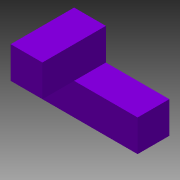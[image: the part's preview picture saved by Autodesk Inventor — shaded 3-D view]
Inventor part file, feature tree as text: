
AUTODESK INVENTOR PART (.ipt)
format: ipt  version: 2013 (Build 170138000, 138)  size: 91,648 bytes
history: native  units: in
note: dims shown in document units (in); Inventor stores cm internally (conversion verified against a paired STEP export)
features: extrude x2, sketch x2
ambient origin geometry x8: Origin, YZ Plane, XZ Plane, XY Plane, X Axis, Y Axis, Z Axis, Center Point
bodies: Solid1 (feature_tree)
feature tree (4):
  extrude  "Extrusion1"  Depth=0.75in
  extrude  "Extrusion2"  Depth=0.75in
  sketch  "Sketch1"  dims[d0=2.25in d2=0.75in]
  sketch  "Sketch2"  dims[d3=0.75in d4=0.0in d5=0.75in d6=1.5in d7=0.75in d8=0.0in]
